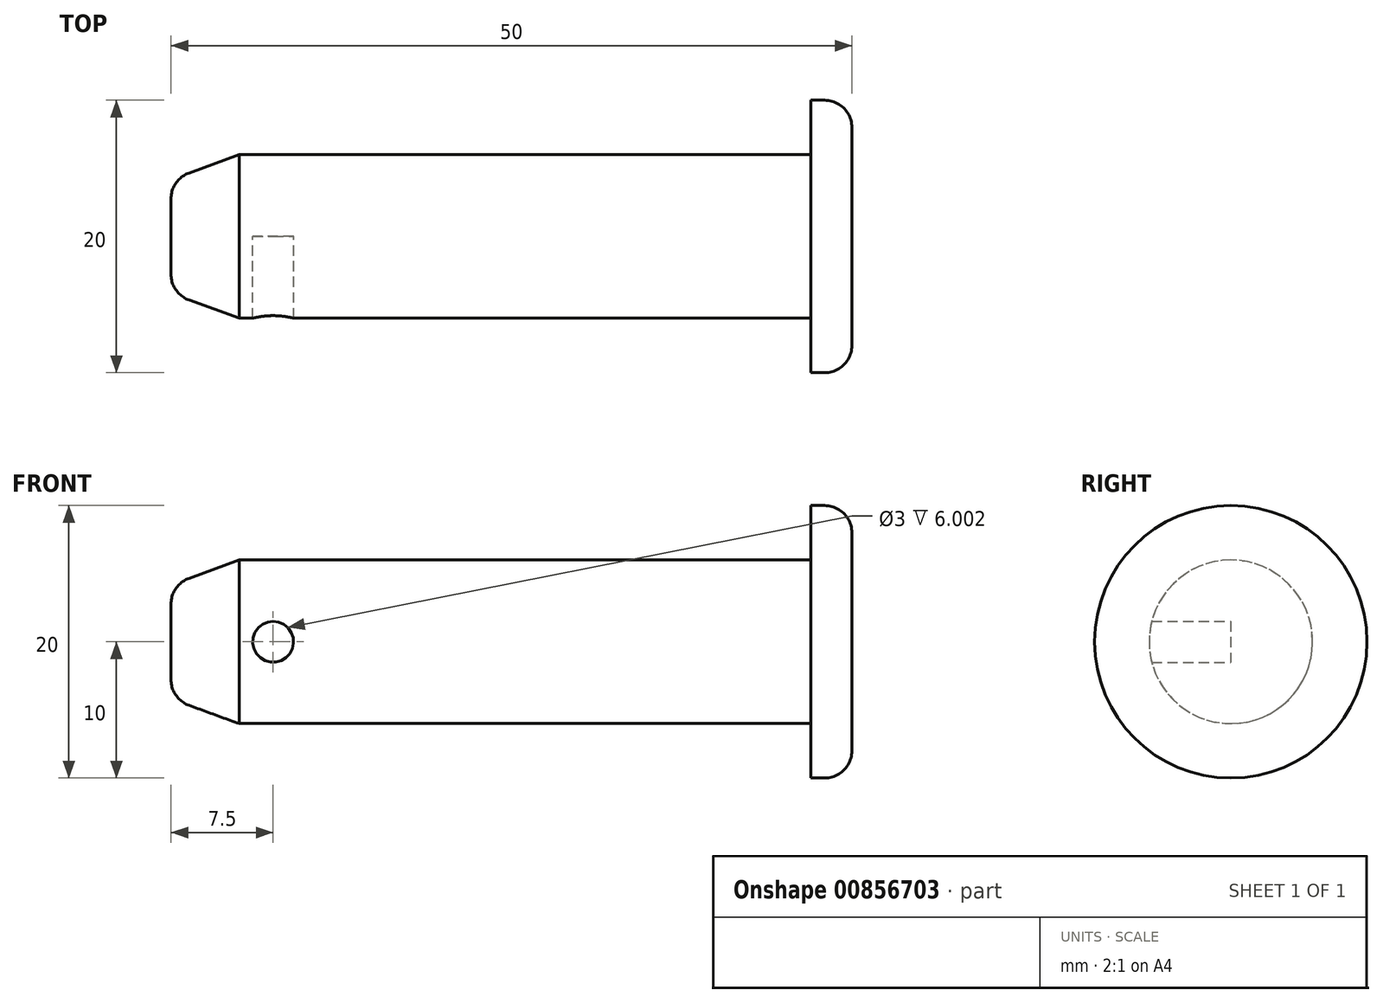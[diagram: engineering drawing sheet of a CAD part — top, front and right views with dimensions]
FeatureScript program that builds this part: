
annotation { "Feature Type Name" : "Feature", "Feature Type Description" : "" }
export const myFeature = defineFeature(function(context is Context, id is Id, definition is map)
    precondition{}
    {
        {
            var Q0;
            Q0=qCreatedBy(makeId("Front.planeOp"),FACE);
            var sketch = newSketch(context, id + "F0", { "sketchPlane" : qUnion([Q0])});
            skLineSegment(sketch, "E0", {"start": v(0, 0) * mm, "end": v(0, 10) * mm});
            skLineSegment(sketch, "E1", {"start": v(0, 10) * mm, "end": v(-3, 10) * mm});
            skLineSegment(sketch, "E2", {"start": v(-3, 10) * mm, "end": v(-3, 6) * mm});
            skLineSegment(sketch, "E3", {"start": v(-3, 6) * mm, "end": v(-50, 6) * mm});
            skLineSegment(sketch, "E4", {"start": v(-50, 6) * mm, "end": v(-50, 0) * mm});
            skLineSegment(sketch, "E5", {"start": v(-50, 0) * mm, "end": v(0, 0) * mm});
            skPoint(sketch, "E6", {"position": v(-42.5, 0) * mm});
            skSolve(sketch);
        }
        {
            var Q0;
            Q0=makeQuery(id+"F0.imprint","IMPRINT",FACE,{"disambiguationData":[TD([[makeQuery(id+"F0.imprint","IMPRINT",EDGE,{"derivedFrom":sQuery(id+"F0.wireOp",EDGE,"E0")}),1.0]])]});
            var Q1;
            Q1=sQuery(id+"F0.wireOp",EDGE,"E5");
            revolve(context, id + "F1", {"surfaceOperationType" : NewSurfaceOperationType.NEW, "entities" : qUnion([Q0]), "axis" : qUnion([Q1]), "revolveType" : RevolveType.FULL});
        }
        {
            var Q0;
            Q0=makeQuery(id+"F1.opRevolve","SWEPT_EDGE",EDGE,{"disambiguationData":[OSD([sQuery(id+"F0.wireOp",EDGE,"E0"),sQuery(id+"F0.wireOp",EDGE,"E1")])]});
            fillet(context, id + "F2", {"entities" : qUnion([Q0]), "radius" : 2 * mm, "tangentPropagation" : true, "allowEdgeOverflow" : false});
        }
        {
            var Q0;
            Q0=makeQuery(id+"F1.opRevolve","SWEPT_EDGE",EDGE,{"disambiguationData":[OSD([sQuery(id+"F0.wireOp",EDGE,"E3"),sQuery(id+"F0.wireOp",EDGE,"E4")])]});
            chamfer(context, id + "F3", {"entities" : qUnion([Q0]), "chamferType" : ChamferType.OFFSET_ANGLE, "width" : 5 * mm, "oppositeDirection" : true, "angle" : 20 * degree, "tangentPropagation" : true});
        }
        {
            var Q0;
            {var subQ0=sQuery(id+"F0.wireOp",EDGE,"E4");Q0=makeQuery(id+"F3.opChamfer","BLEND_EDGE",EDGE,{"blendedFrom":[makeQuery(id+"F1.opRevolve","SWEPT_EDGE",EDGE,{"disambiguationData":[OSD([sQuery(id+"F0.wireOp",EDGE,"E3"),subQ0])]}),makeQuery(id+"F1.opRevolve","SWEPT_FACE",FACE,{"disambiguationData":[OSD([subQ0])]})],"blendedInto":[makeQuery(id+"F1.opRevolve","SWEPT_FACE",FACE,{"disambiguationData":[OSD([subQ0])]})]});}
            fillet(context, id + "F4", {"entities" : qUnion([Q0]), "radius" : 2 * mm, "tangentPropagation" : true, "allowEdgeOverflow" : false});
        }
        {
            var Q0;
            Q0=sQuery(id+"F0.wireOp",VERTEX,"E6");
            var Q1;
            Q1=makeQuery(id+"F1.opRevolve","SWEPT_BODY",BODY,{"disambiguationData":[OSD([sQuery(id+"F0.wireOp",EDGE,"E0"),sQuery(id+"F0.wireOp",EDGE,"E1"),sQuery(id+"F0.wireOp",EDGE,"E2"),sQuery(id+"F0.wireOp",EDGE,"E3"),sQuery(id+"F0.wireOp",EDGE,"E4"),sQuery(id+"F0.wireOp",EDGE,"E5")])]});
            hole(context, id + "F5", {"style" : HoleStyle.SIMPLE, "endStyle" : HoleEndStyle.THROUGH, "oppositeDirection" : true, "holeDiameter" : 3 * mm, "majorDiameter" : 5 * mm, "isTappedThrough" : true, "tappedDepth" : 12 * mm, "tapClearance" : 3, "locations" : qUnion([Q0]), "scope" : qUnion([Q1])});
        }
    });
